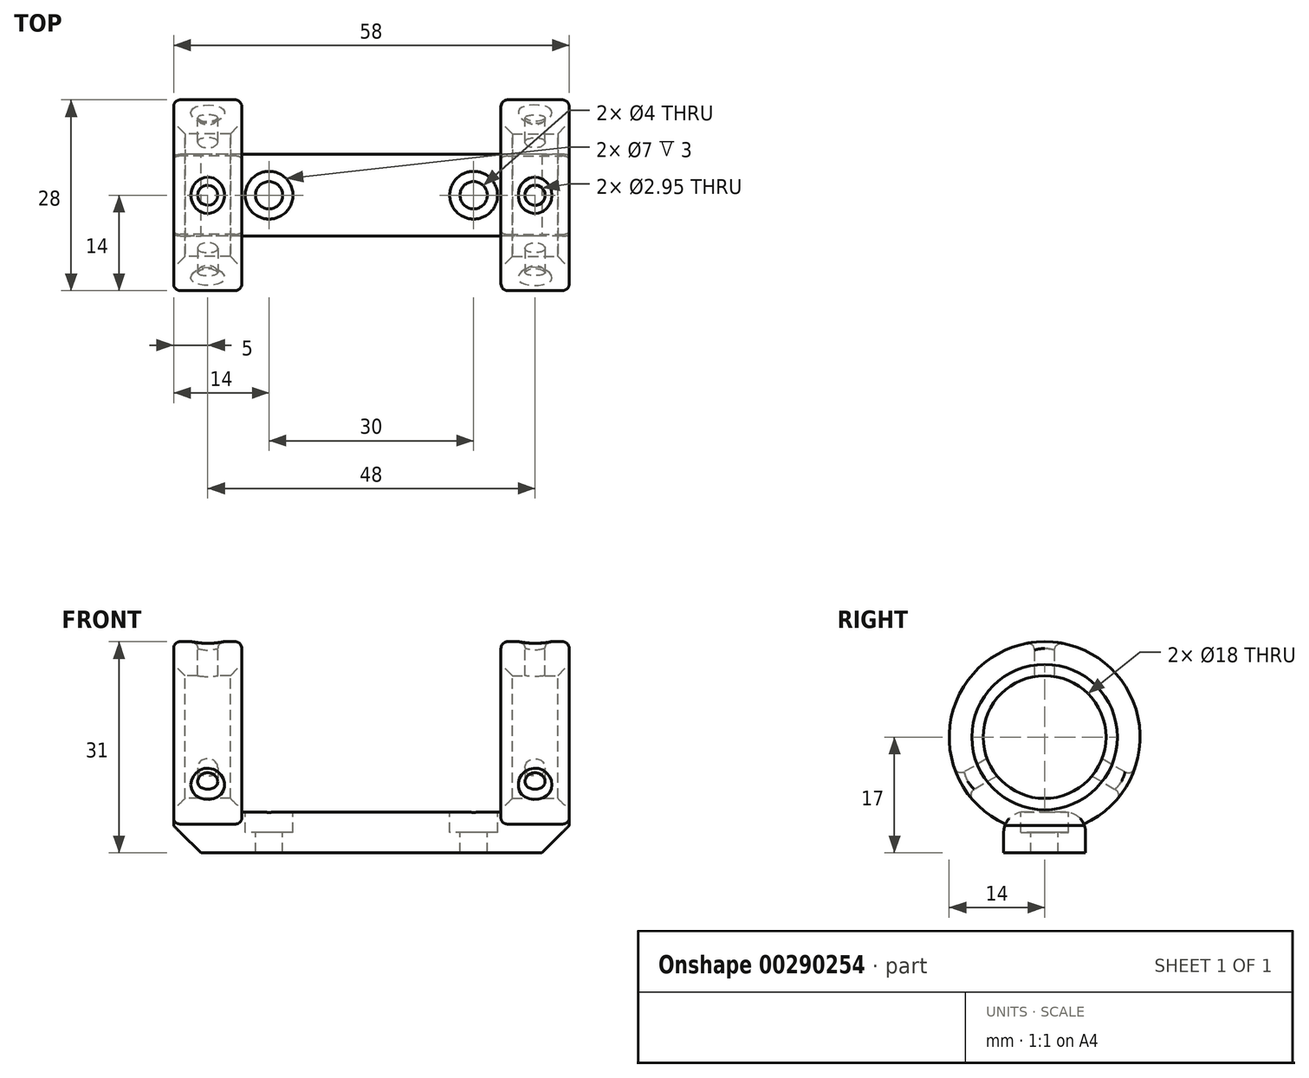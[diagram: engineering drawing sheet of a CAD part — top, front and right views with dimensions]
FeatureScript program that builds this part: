
annotation { "Feature Type Name" : "Feature", "Feature Type Description" : "" }
export const myFeature = defineFeature(function(context is Context, id is Id, definition is map)
    precondition{}
    {
        {
            assignVariable(context, id + "F0", {"name" : "holder_depth_mm", "anyValue" : 10});
        }
        {
            var Q0;
            Q0=qCreatedBy(makeId("Top.planeOp"),FACE);
            var sketch = newSketch(context, id + "F1", { "sketchPlane" : qUnion([Q0])});
            skLineSegment(sketch, "E0.bottom", {"start": v(29, 6) * mm, "end": v(-29, 6) * mm});
            skLineSegment(sketch, "E0.top", {"start": v(29, -6) * mm, "end": v(-29, -6) * mm});
            skLineSegment(sketch, "E0.left", {"start": v(29, 6) * mm, "end": v(29, -6) * mm});
            skLineSegment(sketch, "E0.right", {"start": v(-29, 6) * mm, "end": v(-29, -6) * mm});
            skPoint(sketch, "E0.middle", {"position": v(0, 0) * mm});
            skLineSegment(sketch, "E1", {"start": v(0, 6) * mm, "end": v(0, -7.25) * mm, "construction": true});
            skPoint(sketch, "E1.endSnap0", {"position": v(0, -6) * mm});
            skPoint(sketch, "E2", {"position": v(-15, 0) * mm});
            skPoint(sketch, "E3", {"position": v(15, 0) * mm});
            skSolve(sketch);
        }
        {
            var Q0;
            Q0=makeQuery(id+"F1.imprint","IMPRINT",FACE,{"disambiguationData":[TD([[makeQuery(id+"F1.imprint","IMPRINT",EDGE,{"derivedFrom":sQuery(id+"F1.wireOp",EDGE,"E0.bottom")}),1.0]])]});
            extrude(context, id + "F2", {"entities" : qUnion([Q0]), "oppositeDirection" : true, "depth" : 6 * mm});
        }
        {
            var Q0;
            Q0=sQuery(id+"F1.wireOp",VERTEX,"E2");
            var Q1;
            Q1=sQuery(id+"F1.wireOp",VERTEX,"E3");
            var Q2;
            Q2=makeQuery(id+"F2.opExtrude","SWEPT_BODY",BODY,{"disambiguationData":[OSD([sQuery(id+"F1.wireOp",EDGE,"E0.bottom"),sQuery(id+"F1.wireOp",EDGE,"E0.top"),sQuery(id+"F1.wireOp",EDGE,"E0.left"),sQuery(id+"F1.wireOp",EDGE,"E0.right")])]});
            hole(context, id + "F3", {"style" : HoleStyle.C_BORE, "endStyle" : HoleEndStyle.THROUGH, "holeDiameter" : 4 * mm, "cBoreDiameter" : 7 * mm, "cBoreDepth" : 3 * mm, "tappedDepth" : 12 * mm, "tapClearance" : 3, "locations" : qUnion([Q0, Q1]), "scope" : qUnion([Q2])});
        }
        {
            var Q0;
            Q0=makeQuery(id+"F2.opExtrude","CAP_EDGE",EDGE,{"disambiguationData":[OSD([sQuery(id+"F1.wireOp",EDGE,"E0.left")])],"isStart":false});
            var Q1;
            Q1=makeQuery(id+"F2.opExtrude","CAP_EDGE",EDGE,{"disambiguationData":[OSD([sQuery(id+"F1.wireOp",EDGE,"E0.right")])],"isStart":false});
            chamfer(context, id + "F4", {"entities" : qUnion([Q0, Q1]), "width" : 4 * mm, "tangentPropagation" : true});
        }
        {
            var Q0;
            Q0=makeQuery(id+"F2.opExtrude","SWEPT_FACE",FACE,{"disambiguationData":[OSD([sQuery(id+"F1.wireOp",EDGE,"E0.left")])]});
            var sketch = newSketch(context, id + "F5", { "sketchPlane" : qUnion([Q0])});
            skCircle(sketch, "E4", {"center": v(0, 11) * mm, "radius": 9 * mm});
            skCircle(sketch, "E5", {"center": v(0, 11) * mm, "radius": 14 * mm});
            skLineSegment(sketch, "E6", {"start": v(0, 11) * mm, "end": v(0, 25) * mm, "construction": true});
            skSolve(sketch);
        }
        {
            var Q0;
            Q0=makeQuery(id+"F5.imprint","IMPRINT",FACE,{"disambiguationData":[TD([[makeQuery(id+"F5.imprint","IMPRINT",EDGE,{"derivedFrom":sQuery(id+"F5.wireOp",EDGE,"E4")}),-1.0]])]});
            extrude(context, id + "F6", {"entities" : qUnion([Q0]), "oppositeDirection" : true, "depth" : (getVariable(context, 'holder_depth_mm')) * mm});
        }
        {
            var Q0;
            Q0=makeQuery(id+"F6.opExtrude","SWEPT_FACE",FACE,{"disambiguationData":[OSD([sQuery(id+"F5.wireOp",EDGE,"E4")])]});
            chamfer(context, id + "F7", {"entities" : qUnion([Q0]), "width" : (getVariable(context, 'holder_depth_mm') / 6) * mm, "tangentPropagation" : true});
        }
        {
            var Q0;
            Q0=qCreatedBy(makeId("Top.planeOp"),FACE);
            var Q1;
            Q1=sQuery(id+"F5.wireOp",VERTEX,"E6.end");
            cPlane(context, id + "F8", {"entities" : qUnion([Q0, Q1]), "cplaneType" : CPlaneType.PLANE_POINT, "offset" : (getVariable(context, 'holder_depth_mm') / 2) * mm, "width" : 150 * mm, "height" : 150 * mm});
        }
        {
            var Q0;
            Q0=qCreatedBy(id+"F8.planeOp",FACE);
            var sketch = newSketch(context, id + "F9", { "sketchPlane" : qUnion([Q0])});
            skPoint(sketch, "E7", {"position": v(24, 0) * mm});
            skCircle(sketch, "E8", {"center": v(24, 0) * mm, "radius": 1.48 * mm});
            skLineSegment(sketch, "E9", {"start": v(29, 0) * mm, "end": v(19, 0) * mm});
            skSolve(sketch);
        }
        {
            var Q0;
            Q0 = qSketchRegion(id + "F9", true);
            extrude(context, id + "F10", {"entities" : qUnion([Q0]), "oppositeDirection" : true, "depth" : 10 * mm, "hasSecondDirection" : true, "secondDirectionOppositeDirection" : false, "secondDirectionDepth" : 2 * mm});
        }
        {
            var Q0;
            Q0=makeQuery(id+"F10.opExtrude","SWEPT_BODY",BODY,{"disambiguationData":[OSD([sQuery(id+"F9.wireOp",EDGE,"E8")])]});
            var Q1;
            Q1=sQuery(id+"F5.wireOp",EDGE,"E5");
            circularPattern(context, id + "F11", {"entities" : qUnion([Q0]), "axis" : qUnion([Q1]), "angle" : 360 * degree, "instanceCount" : 3, "equalSpace" : true});
        }
        {
            var Q0;
            Q0=makeQuery(id+"F10.opExtrude","SWEPT_BODY",BODY,{"disambiguationData":[OSD([sQuery(id+"F9.wireOp",EDGE,"E8")])]});
            var Q1;
            Q1=makeQuery(id+"F11.opPattern","COPY",BODY,{"derivedFrom":makeQuery(id+"F10.opExtrude","SWEPT_BODY",BODY,{"disambiguationData":[OSD([sQuery(id+"F9.wireOp",EDGE,"E8")])]}),"instanceName":"2"});
            var Q2;
            Q2=makeQuery(id+"F11.opPattern","COPY",BODY,{"derivedFrom":makeQuery(id+"F10.opExtrude","SWEPT_BODY",BODY,{"disambiguationData":[OSD([sQuery(id+"F9.wireOp",EDGE,"E8")])]}),"instanceName":"1"});
            var Q3;
            Q3=makeQuery(id+"F6.opExtrude","SWEPT_BODY",BODY,{"disambiguationData":[OSD([sQuery(id+"F1.wireOp",EDGE,"E0.bottom"),sQuery(id+"F1.wireOp",EDGE,"E0.top"),sQuery(id+"F1.wireOp",EDGE,"E0.left"),sQuery(id+"F5.wireOp",EDGE,"E4"),sQuery(id+"F5.wireOp",EDGE,"E5")])]});
            booleanBodies(context, id + "F12", {"operationType" : BooleanOperationType.SUBTRACTION, "tools" : qUnion([Q0, Q1, Q2]), "targets" : qUnion([Q3])});
        }
        {
            var Q0;
            Q0=makeQuery(id+"F12.opBoolean","INTERSECT",EDGE,{"derivedFrom":[makeQuery(id+"F6.opExtrude","SWEPT_FACE",FACE,{"disambiguationData":[OSD([sQuery(id+"F5.wireOp",EDGE,"E5")])]}),makeQuery(id+"F10.opExtrude","SWEPT_FACE",FACE,{"disambiguationData":[OSD([sQuery(id+"F9.wireOp",EDGE,"E8")])]})]});
            var Q1;
            Q1=makeQuery(id+"F6.opExtrude","CAP_EDGE",EDGE,{"disambiguationData":[OSD([sQuery(id+"F5.wireOp",EDGE,"E5")])],"isStart":false});
            var Q2;
            Q2=makeQuery(id+"F6.opExtrude","CAP_EDGE",EDGE,{"disambiguationData":[OSD([sQuery(id+"F5.wireOp",EDGE,"E5")])],"isStart":true});
            var Q3;
            Q3=makeQuery(id+"F12.opBoolean","INTERSECT",EDGE,{"derivedFrom":[makeQuery(id+"F6.opExtrude","SWEPT_FACE",FACE,{"disambiguationData":[OSD([sQuery(id+"F5.wireOp",EDGE,"E5")])]}),makeQuery(id+"F11.opPattern","COPY",FACE,{"derivedFrom":makeQuery(id+"F10.opExtrude","SWEPT_FACE",FACE,{"disambiguationData":[OSD([sQuery(id+"F9.wireOp",EDGE,"E8")])]}),"instanceName":"1"})]});
            var Q4;
            Q4=makeQuery(id+"F12.opBoolean","INTERSECT",EDGE,{"derivedFrom":[makeQuery(id+"F6.opExtrude","SWEPT_FACE",FACE,{"disambiguationData":[OSD([sQuery(id+"F5.wireOp",EDGE,"E5")])]}),makeQuery(id+"F11.opPattern","COPY",FACE,{"derivedFrom":makeQuery(id+"F10.opExtrude","SWEPT_FACE",FACE,{"disambiguationData":[OSD([sQuery(id+"F9.wireOp",EDGE,"E8")])]}),"instanceName":"2"})]});
            var Q5;
            Q5=makeQuery(id+"F3.hole-0.boolean.opBoolean","COPY",EDGE,{"derivedFrom":makeQuery(id+"F3.hole-0.opRevolve","SWEPT_EDGE",EDGE,{"disambiguationData":[OSD([sQuery(id+"F3.hole-0.sketch.wireOp",EDGE,"cbore_start_line_2"),sQuery(id+"F3.hole-0.sketch.wireOp",EDGE,"cbore_start_line_3")])]})});
            var Q6;
            Q6=makeQuery(id+"F3.hole-1.boolean.opBoolean","COPY",EDGE,{"derivedFrom":makeQuery(id+"F3.hole-1.opRevolve","SWEPT_EDGE",EDGE,{"disambiguationData":[OSD([sQuery(id+"F3.hole-1.sketch.wireOp",EDGE,"cbore_start_line_2"),sQuery(id+"F3.hole-1.sketch.wireOp",EDGE,"cbore_start_line_3")])]})});
            fillet(context, id + "F13", {"entities" : qUnion([Q0, Q1, Q2, Q3, Q4, Q5, Q6]), "radius" : 1 * mm, "tangentPropagation" : true, "allowEdgeOverflow" : false});
        }
        {
            var Q0;
            Q0=makeQuery(id+"F6.opExtrude","SWEPT_BODY",BODY,{"disambiguationData":[OSD([sQuery(id+"F1.wireOp",EDGE,"E0.bottom"),sQuery(id+"F1.wireOp",EDGE,"E0.top"),sQuery(id+"F1.wireOp",EDGE,"E0.left"),sQuery(id+"F5.wireOp",EDGE,"E4"),sQuery(id+"F5.wireOp",EDGE,"E5")])]});
            var Q1;
            Q1=qCreatedBy(makeId("Right.planeOp"),FACE);
            mirror(context, id + "F14", {"operationType" : NewBodyOperationType.ADD, "entities" : qUnion([Q0]), "mirrorPlane" : qUnion([Q1])});
        }
        {
            var Q0;
            Q0=makeQuery(id+"F2.opExtrude","CAP_EDGE",EDGE,{"disambiguationData":[OSD([sQuery(id+"F1.wireOp",EDGE,"E0.top")])],"isStart":true});
            var Q1;
            Q1=makeQuery(id+"F2.opExtrude","CAP_EDGE",EDGE,{"disambiguationData":[OSD([sQuery(id+"F1.wireOp",EDGE,"E0.bottom")])],"isStart":true});
            fillet(context, id + "F15", {"entities" : qUnion([Q0, Q1]), "radius" : 3 * mm, "tangentPropagation" : true, "allowEdgeOverflow" : false});
        }
    });
